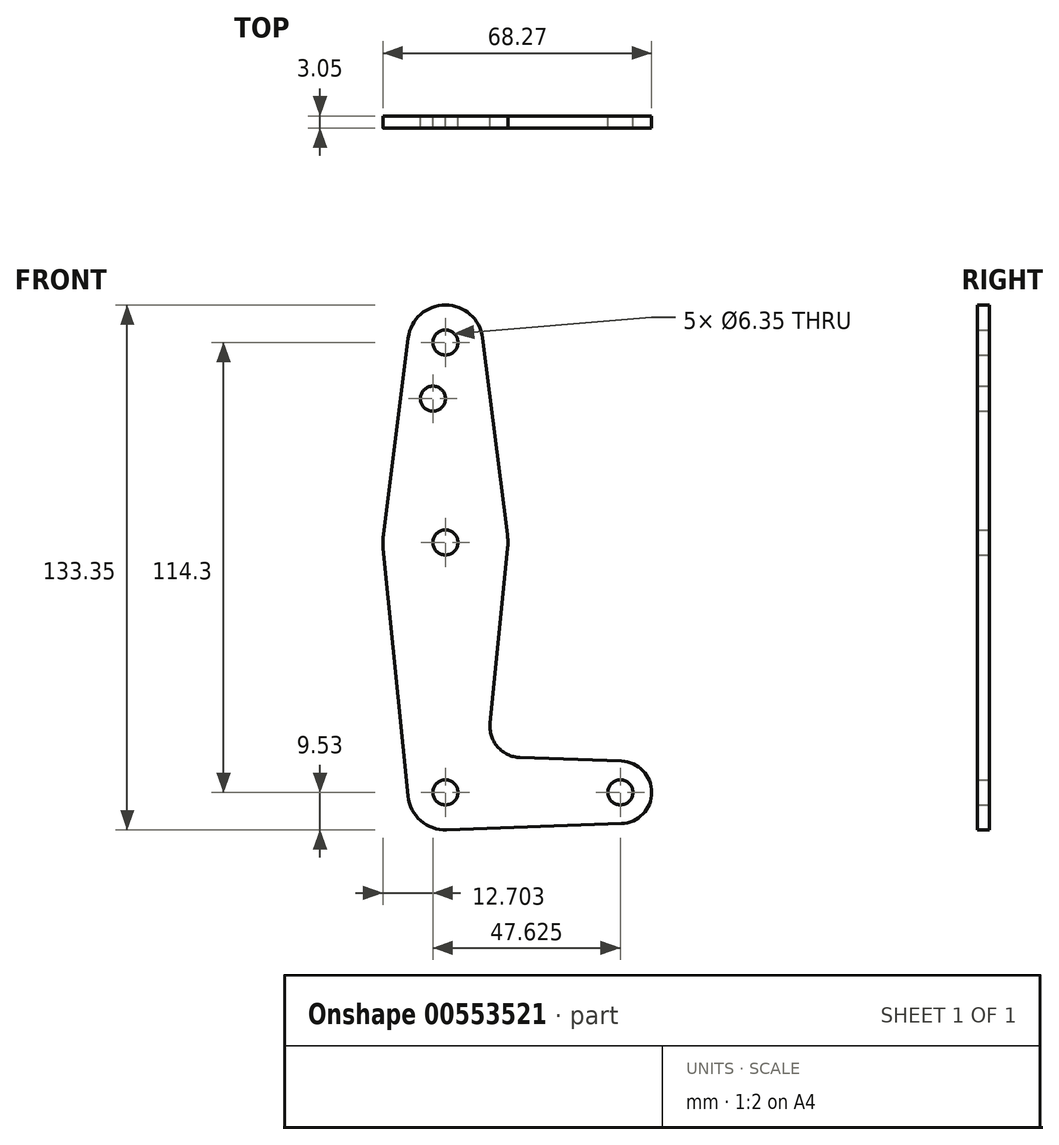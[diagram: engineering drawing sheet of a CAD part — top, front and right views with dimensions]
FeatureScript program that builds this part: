
annotation { "Feature Type Name" : "Feature", "Feature Type Description" : "" }
export const myFeature = defineFeature(function(context is Context, id is Id, definition is map)
    precondition{}
    {
        {
            var Q0;
            Q0=qCreatedBy(makeId("Front.planeOp"),FACE);
            var sketch = newSketch(context, id + "F0", { "sketchPlane" : qUnion([Q0])});
            skLineSegment(sketch, "E0", {"start": v(-153.57, 8.82) * mm, "end": v(-153.57, -102.3) * mm, "construction": true});
            skLineSegment(sketch, "E1", {"start": v(-153.57, -105.48) * mm, "end": v(-109.12, -105.48) * mm, "construction": true});
            skCircle(sketch, "E2", {"center": v(-153.57, 8.82) * mm, "radius": 9.53 * mm});
            skCircle(sketch, "E3", {"center": v(-153.57, -105.48) * mm, "radius": 9.53 * mm});
            skCircle(sketch, "E4", {"center": v(-109.12, -105.48) * mm, "radius": 7.94 * mm});
            skCircle(sketch, "E5", {"center": v(-153.57, -41.98) * mm, "radius": 15.88 * mm});
            skLineSegment(sketch, "E6", {"start": v(-137.82, -40) * mm, "end": v(-144.12, 10.01) * mm});
            skLineSegment(sketch, "E7", {"start": v(-163.02, 10.01) * mm, "end": v(-169.32, -40) * mm});
            skLineSegment(sketch, "E8", {"start": v(-169.37, -43.57) * mm, "end": v(-163.05, -106.43) * mm});
            skLineSegment(sketch, "E9", {"start": v(-137.78, -43.57) * mm, "end": v(-142.23, -87.89) * mm});
            skCircle(sketch, "E10", {"center": v(-156.75, -5.45) * mm, "radius": 3.18 * mm});
            skCircle(sketch, "E11", {"center": v(-153.57, -41.98) * mm, "radius": 3.18 * mm});
            skCircle(sketch, "E12", {"center": v(-153.57, 8.82) * mm, "radius": 3.18 * mm});
            skCircle(sketch, "E13", {"center": v(-153.57, -105.48) * mm, "radius": 3.18 * mm});
            skCircle(sketch, "E14", {"center": v(-109.12, -105.48) * mm, "radius": 3.18 * mm});
            skLineSegment(sketch, "E15", {"start": v(-134.6, -96.63) * mm, "end": v(-108.84, -97.55) * mm});
            skLineSegment(sketch, "E16", {"start": v(-153.23, -115) * mm, "end": v(-108.84, -113.41) * mm});
            skLineSegment(sketch, "E17", {"start": v(-120.83, -113.84) * mm, "end": v(-108.84, -113.41) * mm});
            skArc(sketch, "E18.filletArc", {"start": v(-142.23, -87.89) * mm, "mid": v(-140.31, -93.9) * mm, "end": v(-134.6, -96.63) * mm});
            skSolve(sketch);
        }
        {
            var Q0;
            Q0 = qSketchRegion(id + "F0", true);
            extrude(context, id + "F1", {"entities" : qUnion([Q0]), "depth" : 3.05 * mm, "offsetDistance" : 25.4 * mm});
        }
    });
